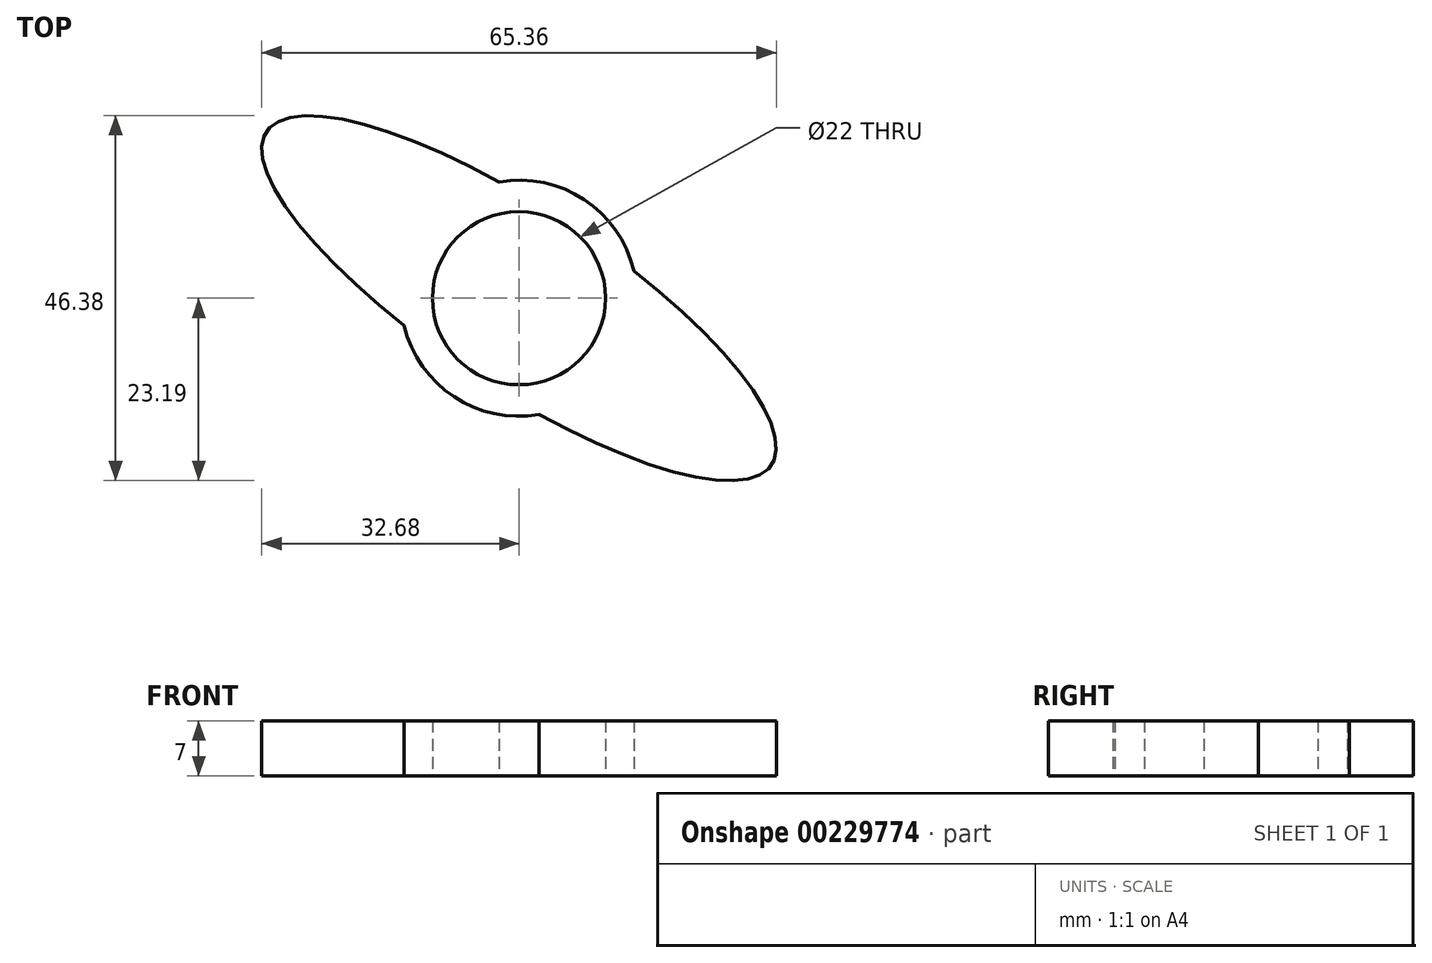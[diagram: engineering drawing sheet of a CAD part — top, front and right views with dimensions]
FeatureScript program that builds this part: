
annotation { "Feature Type Name" : "Feature", "Feature Type Description" : "" }
export const myFeature = defineFeature(function(context is Context, id is Id, definition is map)
    precondition{}
    {
        {
            var Q0;
            Q0=qCreatedBy(makeId("Top.planeOp"),FACE);
            var sketch = newSketch(context, id + "F0", { "sketchPlane" : qUnion([Q0])});
            skCircle(sketch, "E0", {"center": v(0, 0) * mm, "radius": 11 * mm});
            skCircle(sketch, "E1", {"center": v(0, 0) * mm, "radius": 15 * mm});
            skPoint(sketch, "E2", {"position": v(-18.8, 17.13) * mm});
            skPoint(sketch, "E3", {"position": v(20.33, -15.27) * mm});
            skSolve(sketch);
        }
        {
            var Q0;
            Q0=makeQuery(id+"F0.imprint","IMPRINT",FACE,{"disambiguationData":[TD([[makeQuery(id+"F0.imprint","IMPRINT",EDGE,{"derivedFrom":sQuery(id+"F0.wireOp",EDGE,"E0")}),-1.0]])]});
            extrude(context, id + "F1", {"entities" : qUnion([Q0]), "depth" : 7 * mm, "offsetDistance" : 25.4 * mm});
        }
        {
            var Q0;
            Q0=qCreatedBy(makeId("Top.planeOp"),FACE);
            var sketch = newSketch(context, id + "F2", { "sketchPlane" : qUnion([Q0])});
            skEllipse(sketch, "E4", {"center": v(0, 0) * mm, "majorRadius": 38.43 * mm, "minorRadius": 11.34 * mm, "majorAxis": v(0.83, -0.55)});
            skSolve(sketch);
        }
        {
            var Q0;
            Q0 = qSketchRegion(id + "F2", true);
            extrude(context, id + "F3", {"entities" : qUnion([Q0]), "operationType" : NewBodyOperationType.ADD, "depth" : 7 * mm, "offsetDistance" : 25.4 * mm});
        }
        {
            var Q0;
            Q0=makeQuery(id+"F0.imprint","IMPRINT",FACE,{"disambiguationData":[TD([[makeQuery(id+"F0.imprint","IMPRINT",EDGE,{"derivedFrom":sQuery(id+"F0.wireOp",EDGE,"E0")}),1.0]])]});
            extrude(context, id + "F4", {"entities" : qUnion([Q0]), "operationType" : NewBodyOperationType.REMOVE, "depth" : 25.4 * mm, "offsetDistance" : 25.4 * mm});
        }
    });
